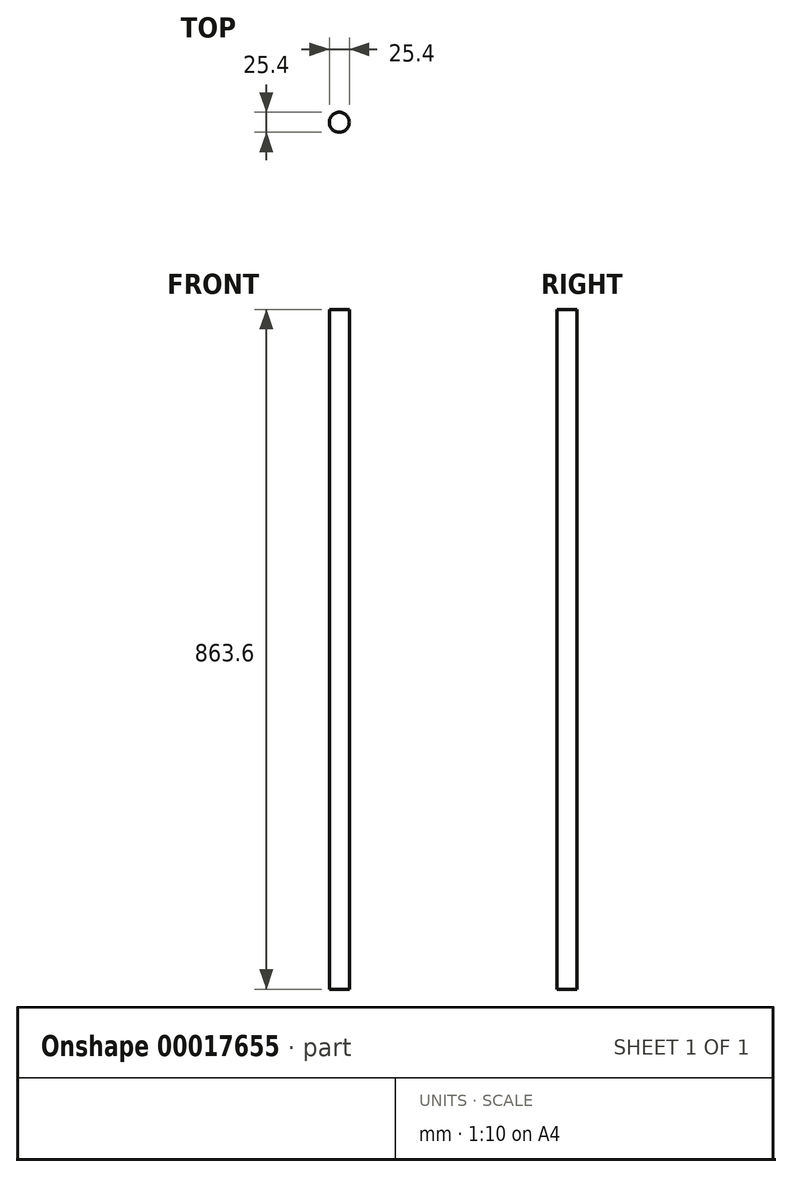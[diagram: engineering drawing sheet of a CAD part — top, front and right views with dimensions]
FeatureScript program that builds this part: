
annotation { "Feature Type Name" : "Feature", "Feature Type Description" : "" }
export const myFeature = defineFeature(function(context is Context, id is Id, definition is map)
    precondition{}
    {
        {
            var Q0;
            Q0=qCreatedBy(makeId("Top.planeOp"),FACE);
            var sketch = newSketch(context, id + "F0", { "sketchPlane" : qUnion([Q0])});
            skCircle(sketch, "E0", {"center": v(0, 0) * mm, "radius": 12.7 * mm});
            skSolve(sketch);
        }
        {
            var Q0;
            Q0=makeQuery(id+"F0.imprint","IMPRINT",FACE,{"disambiguationData":[TD([[makeQuery(id+"F0.imprint","IMPRINT",EDGE,{"derivedFrom":sQuery(id+"F0.wireOp",EDGE,"E0")}),1.0]])]});
            extrude(context, id + "F1", {"entities" : qUnion([Q0]), "depth" : 863.6 * mm});
        }
    });
